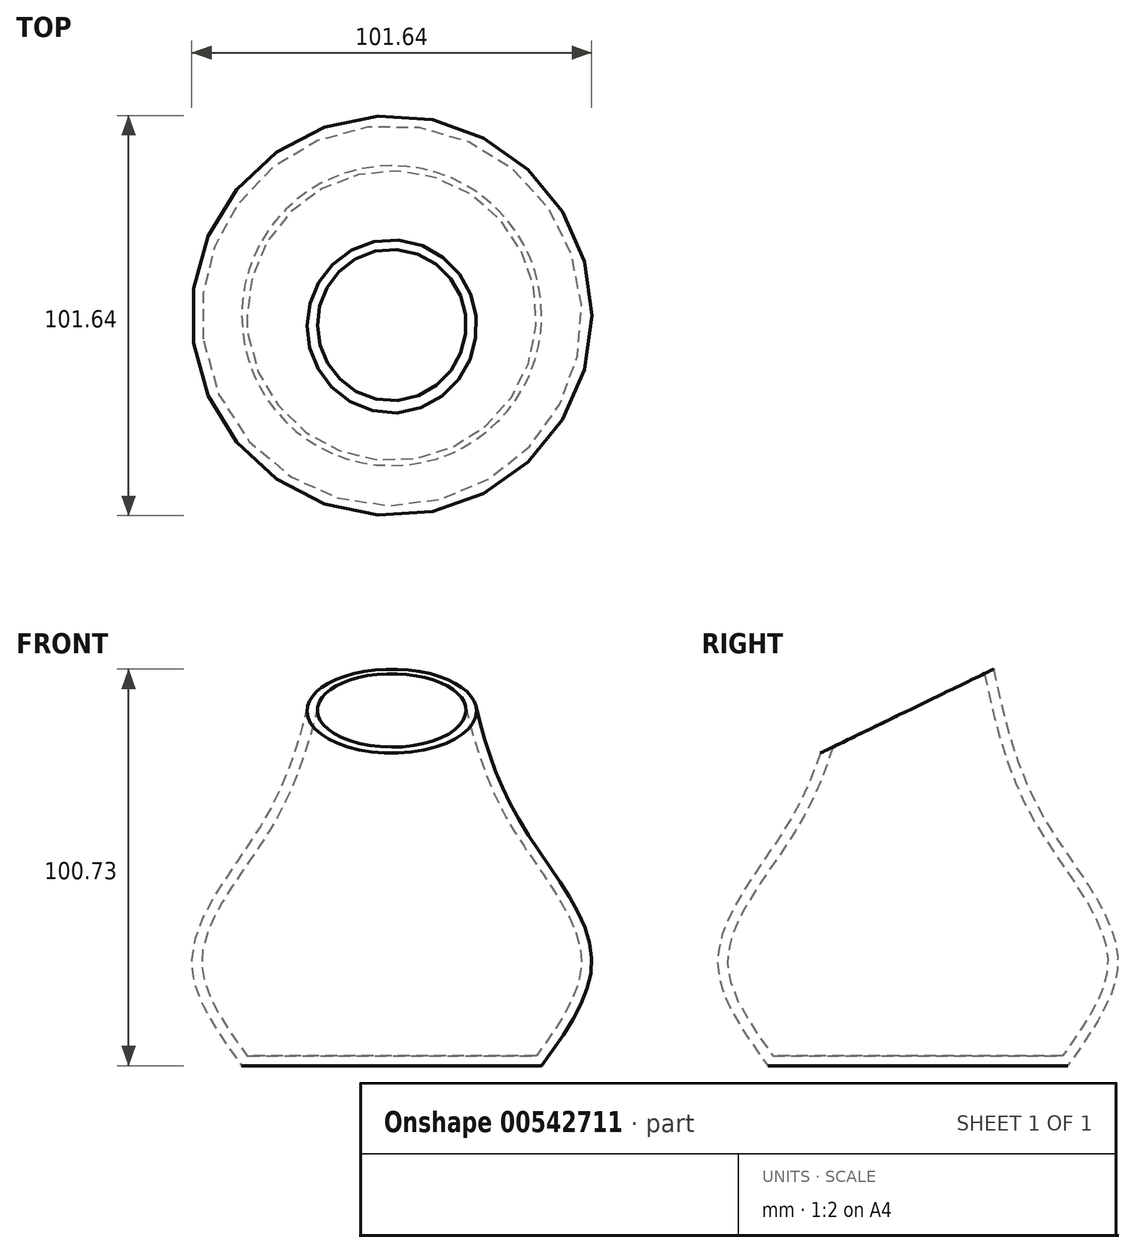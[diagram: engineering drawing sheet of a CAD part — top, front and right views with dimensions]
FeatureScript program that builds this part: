
annotation { "Feature Type Name" : "Feature", "Feature Type Description" : "" }
export const myFeature = defineFeature(function(context is Context, id is Id, definition is map)
    precondition{}
    {
        {
            var Q0;
            Q0=qCreatedBy(makeId("Top.planeOp"),FACE);
            var sketch = newSketch(context, id + "F0", { "sketchPlane" : qUnion([Q0])});
            skCircle(sketch, "E0", {"center": v(0, 0) * mm, "radius": 38.1 * mm});
            skSolve(sketch);
        }
        {
            var Q0;
            Q0=qCreatedBy(makeId("Top.planeOp"),FACE);
            cPlane(context, id + "F1", {"entities" : qUnion([Q0]), "cplaneType" : CPlaneType.OFFSET, "offset" : 25.4 * mm, "width" : 152.4 * mm, "height" : 152.4 * mm});
        }
        {
            var Q0;
            Q0=qCreatedBy(id+"F1.planeOp",FACE);
            var sketch = newSketch(context, id + "F2", { "sketchPlane" : qUnion([Q0])});
            skCircle(sketch, "E1", {"center": v(0, 0) * mm, "radius": 50.8 * mm});
            skSolve(sketch);
        }
        {
            var Q0;
            Q0=qCreatedBy(id+"F1.planeOp",FACE);
            cPlane(context, id + "F3", {"entities" : qUnion([Q0]), "cplaneType" : CPlaneType.OFFSET, "offset" : 38.1 * mm, "width" : 152.4 * mm, "height" : 152.4 * mm});
        }
        {
            var Q0;
            Q0=qCreatedBy(id+"F3.planeOp",FACE);
            var sketch = newSketch(context, id + "F4", { "sketchPlane" : qUnion([Q0])});
            skCircle(sketch, "E2", {"center": v(0, 0) * mm, "radius": 31.75 * mm});
            skSolve(sketch);
        }
        {
            var Q0;
            Q0=qCreatedBy(id+"F3.planeOp",FACE);
            cPlane(context, id + "F5", {"entities" : qUnion([Q0]), "cplaneType" : CPlaneType.OFFSET, "offset" : 38.1 * mm, "width" : 152.4 * mm, "height" : 152.4 * mm});
        }
        {
            var Q0;
            Q0=qCreatedBy(id+"F5.planeOp",FACE);
            var sketch = newSketch(context, id + "F6", { "sketchPlane" : qUnion([Q0])});
            skCircle(sketch, "E3", {"center": v(0, 0) * mm, "radius": 19.05 * mm});
            skSolve(sketch);
        }
        {
            var Q0;
            Q0=makeQuery(id+"F0.imprint","IMPRINT",FACE,{"disambiguationData":[TD([[makeQuery(id+"F0.imprint","IMPRINT",EDGE,{"derivedFrom":sQuery(id+"F0.wireOp",EDGE,"E0")}),1.0]])]});
            var Q1;
            Q1=makeQuery(id+"F2.imprint","IMPRINT",FACE,{"disambiguationData":[TD([[makeQuery(id+"F2.imprint","IMPRINT",EDGE,{"derivedFrom":sQuery(id+"F2.wireOp",EDGE,"E1")}),1.0]])]});
            var Q2;
            Q2=makeQuery(id+"F4.imprint","IMPRINT",FACE,{"disambiguationData":[TD([[makeQuery(id+"F4.imprint","IMPRINT",EDGE,{"derivedFrom":sQuery(id+"F4.wireOp",EDGE,"E2")}),1.0]])]});
            var Q3;
            Q3=makeQuery(id+"F6.imprint","IMPRINT",FACE,{"disambiguationData":[TD([[makeQuery(id+"F6.imprint","IMPRINT",EDGE,{"derivedFrom":sQuery(id+"F6.wireOp",EDGE,"E3")}),1.0]])]});
            loft(context, id + "F7", {"sheetProfilesArray" : [{ "sheetProfileEntities" : qUnion([Q0]) }, { "sheetProfileEntities" : qUnion([Q1]) }, { "sheetProfileEntities" : qUnion([Q2]) }, { "sheetProfileEntities" : qUnion([Q3]) }]});
        }
        {
            var Q0;
            Q0=qCreatedBy(makeId("Right.planeOp"),FACE);
            var sketch = newSketch(context, id + "F8", { "sketchPlane" : qUnion([Q0])});
            skLineSegment(sketch, "E4", {"start": v(-34.69, 74.6) * mm, "end": v(47.7, 114.52) * mm});
            skLineSegment(sketch, "E5", {"start": v(47.7, 114.52) * mm, "end": v(-61.44, 114.52) * mm});
            skLineSegment(sketch, "E6", {"start": v(-61.44, 114.52) * mm, "end": v(-34.69, 74.6) * mm});
            skSolve(sketch);
        }
        {
            var Q0;
            Q0 = qSketchRegion(id + "F8", true);
            extrude(context, id + "F9", {"entities" : qUnion([Q0]), "operationType" : NewBodyOperationType.REMOVE, "endBound" : BoundingType.SYMMETRIC, "oppositeDirection" : true, "depth" : 86.87 * mm, "offsetDistance" : 25.4 * mm});
        }
        {
            var Q0;
            Q0=makeQuery(id+"F9.boolean.opBoolean","COPY",FACE,{"derivedFrom":makeQuery(id+"F9.opExtrude","SWEPT_FACE",FACE,{"disambiguationData":[OSD([sQuery(id+"F8.wireOp",EDGE,"E4")])]})});
            shell(context, id + "F10", {"entities" : qUnion([Q0]), "thickness" : 2.54 * mm});
        }
    });
